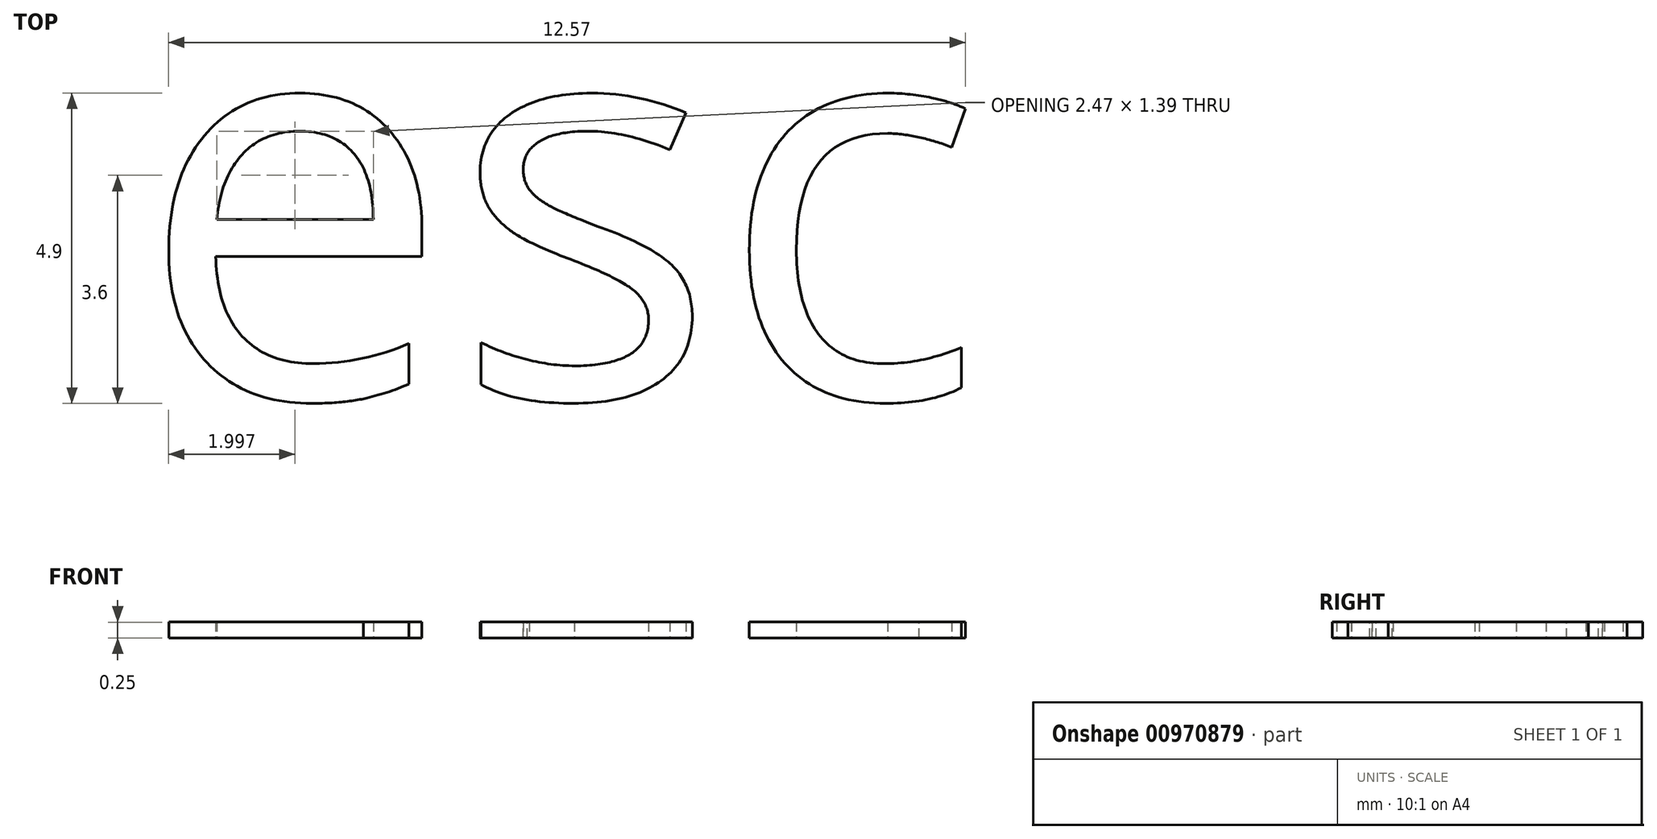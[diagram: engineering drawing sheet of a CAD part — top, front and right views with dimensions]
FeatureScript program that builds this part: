
annotation { "Feature Type Name" : "Feature", "Feature Type Description" : "" }
export const myFeature = defineFeature(function(context is Context, id is Id, definition is map)
    precondition{}
    {
        {
            var Q0;
            Q0=qCreatedBy(makeId("Top.planeOp"),FACE);
            var sketch = newSketch(context, id + "F0", { "sketchPlane" : qUnion([Q0])});
            skText(sketch, "E0", { "text": "esc\n", "fontName": "OpenSans-Regular.ttf"});
            const initialGuessF0  = {"E0": [-0.03407, 0.01259, 1, 0, 0.00635]};
            skSetInitialGuess(sketch, initialGuessF0);
            skSolve(sketch);
        }
        {
            var Q0;
            Q0=qSketchRegion(id+"F0",true);
            extrude(context, id + "F1", {"entities" : qUnion([Q0]), "depth" : 0.25 * mm, "offsetDistance" : 25.4 * mm});
        }
    });
